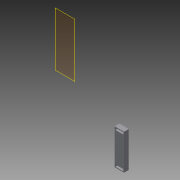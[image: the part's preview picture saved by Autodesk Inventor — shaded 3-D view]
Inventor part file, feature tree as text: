
AUTODESK INVENTOR PART (.ipt)
format: ipt  version: 2015 (Build 190159000, 159)  size: 88,576 bytes
history: native  units: in
note: dims shown in document units (in); Inventor stores cm internally (conversion verified against a paired STEP export)
features: extrude x2, sketch x2, reference x2, plane x1
ambient origin geometry x8: Origin, YZ Plane, XZ Plane, XY Plane, X Axis, Y Axis, Z Axis, Center Point
bodies: Solid1 (feature_tree)
feature tree (7):
  plane  "Work Plane1"
  extrude  "Extrusion1"  Depth=0.1in TaperAngle=0.0deg
  extrude  "Extrusion2"  [1 undecoded]
  sketch  "Sketch1"  dims[d2=0.5in d3=0.0in d4=0.1in d5=0.0in]
  reference  "Reference1"
  reference  "Reference2"
  sketch  "Sketch2"
note: 1 required parameter value undecoded (feature->parameter linkage not recoverable at this tier; creation-order binding heuristic only, values carry confidence <= 0.55)
